# Revit family: LAMP_MUN LIGHT 300 SUSPENDED
name_source: partatom
category: Modelos genéricos
revit_build: Autodesk Revit 2015 (Build: 20140606_1530(x64)
units: mm (PartAtom-declared; Revit-internal decimal feet)

## types (4) — shared parameters
CRI = 80
Diameter = 300 mm
Elevación por defecto = 1219 mm
Fabricante = LAMP
Gear = Electronic
Height = 64 mm  [stored 0.209974 ft]
IEE = A+
Installation instructions = https://www.lamp.es
Insulation class = I
LED Lifetime = 50.000 L80 B10
Lamp = LOW POWER LED
Last update = 11/11/2020
Luminaire type = Indoor - Downlight
MacAdam = <3
Manufacturer URL = http://www.lamp.es
Manufacturer country = Spain
Manufacturer name = LAMP
Photometric web file = Cuerpo Mun light 300 : 716LM 3000 GRAPHITE
Plum = 9 W
Power = 8 W
Power Supply = 220-240V 50-60Hz
Product URL = https://www.lamp.es
Product datasheet = http://www.lamp.es
Protection rating = IP20 / IK08
Type = LOW POWER OSRAM
Weight = 2.68 kg

## per-type parameters (varying)
| type | Descripción | Efficacy | Finish | Initial color | Initial intensity | Modelo | Product code |
| 716LM 4000 GRAPHITE | MUN LIGHT SUS Ø300 1000 NW GRH. | 77 lm/W | Texturised matte graphite | 4000 K | 716 lm | ML1300SU10840NB | ML1300SU10840NB |
| 716LM 3000 GRAPHITE | MUN LIGHT SUS Ø300 1000 WW GRH. | 77 lm/W | Texturised matte graphite | 3000 K | 716 lm | ML1300SU10830NB | ML1300SU10830NB |
| 761LM 4000 WHITE | MUN LIGHT SUS Ø300 1000 NW WH. | 82 lm/W | Texturised matte white | 4000 K | 761 lm | ML1300SU10840NW | ML1300SU10840NW |
| 761LM 3000 WHITE | MUN LIGHT SUS Ø300 1000 WW WH. | 82 lm/W | Texturised matte white | 3000 K | 761 lm | ML1300SU10830NW | ML1300SU10830NW |

note: [stored X ft] marks values corroborated as IEEE doubles in the binary element streams (Revit-internal decimal feet)
